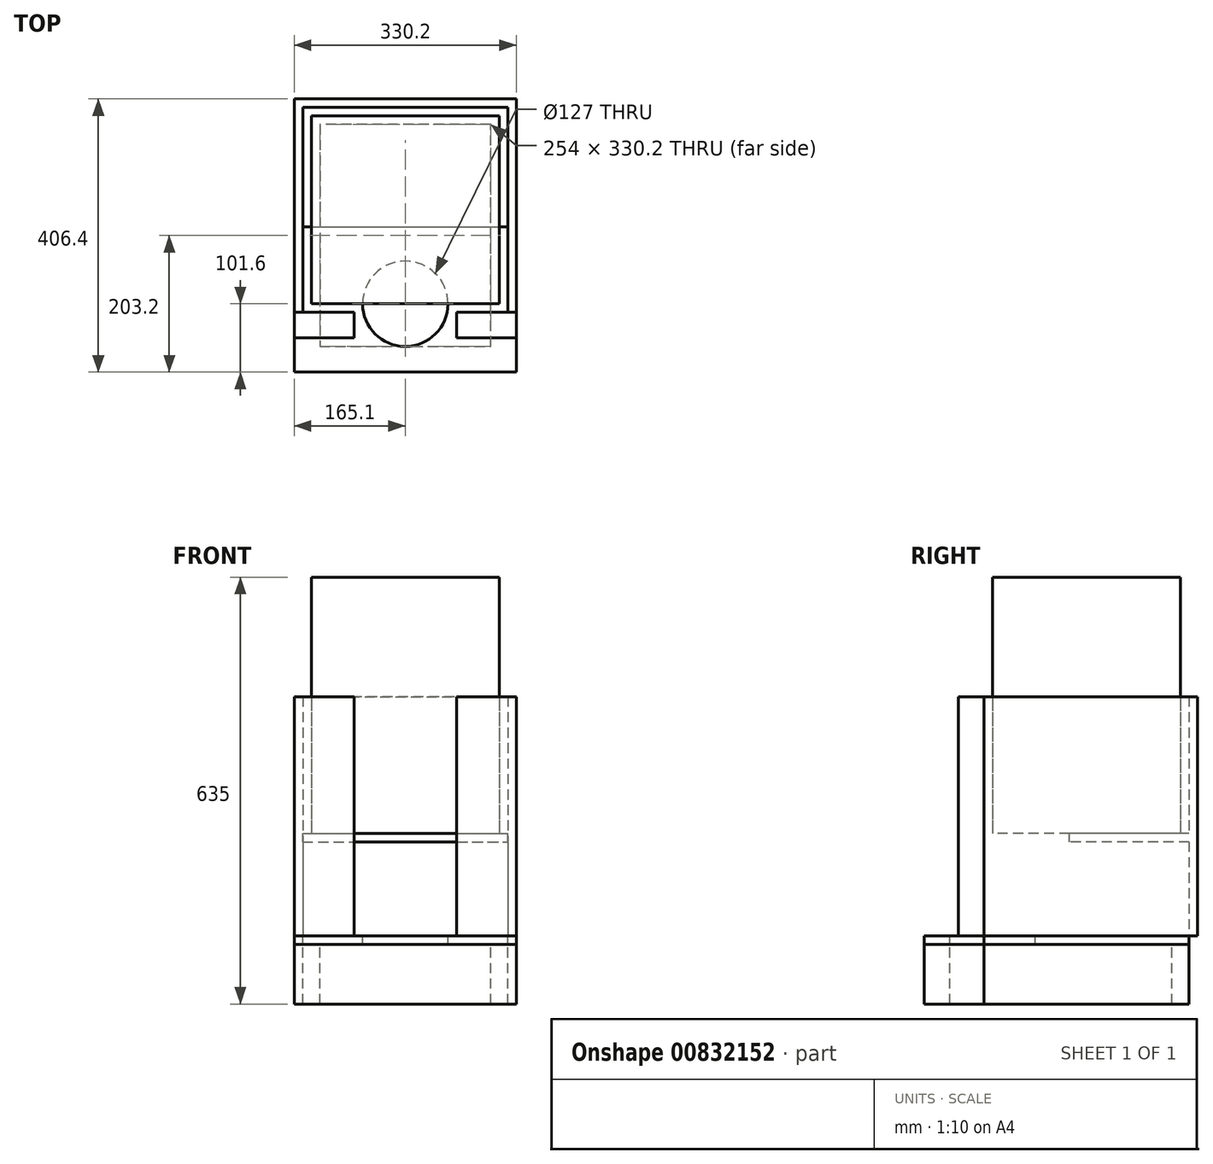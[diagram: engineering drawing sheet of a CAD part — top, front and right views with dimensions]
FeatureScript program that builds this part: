
annotation { "Feature Type Name" : "Feature", "Feature Type Description" : "" }
export const myFeature = defineFeature(function(context is Context, id is Id, definition is map)
    precondition{}
    {
        {
            var Q0;
            Q0=qCreatedBy(makeId("Top.planeOp"),FACE);
            var sketch = newSketch(context, id + "F0", { "sketchPlane" : qUnion([Q0])});
            skLineSegment(sketch, "E0", {"start": v(-165.1, 158.75) * mm, "end": v(-165.1, -158.75) * mm});
            skLineSegment(sketch, "E1", {"start": v(-152.4, -158.75) * mm, "end": v(-152.4, 146.05) * mm});
            skLineSegment(sketch, "E2", {"start": v(-152.4, 146.05) * mm, "end": v(152.4, 146.05) * mm});
            skLineSegment(sketch, "E3", {"start": v(152.4, 146.05) * mm, "end": v(152.4, -158.75) * mm});
            skLineSegment(sketch, "E4", {"start": v(165.1, -158.75) * mm, "end": v(165.1, 158.75) * mm});
            skLineSegment(sketch, "E5", {"start": v(165.1, 158.75) * mm, "end": v(-165.1, 158.75) * mm});
            skLineSegment(sketch, "E6", {"start": v(-152.4, 146.05) * mm, "end": v(-165.1, 146.05) * mm, "construction": true});
            skLineSegment(sketch, "E7", {"start": v(-152.4, 146.05) * mm, "end": v(-152.4, 158.75) * mm, "construction": true});
            skLineSegment(sketch, "E8", {"start": v(152.4, 146.05) * mm, "end": v(165.1, 146.05) * mm, "construction": true});
            skLineSegment(sketch, "E9", {"start": v(165.1, -158.75) * mm, "end": v(152.4, -158.75) * mm});
            skLineSegment(sketch, "E10", {"start": v(-152.4, -158.75) * mm, "end": v(-165.1, -158.75) * mm});
            skSolve(sketch);
        }
        {
            var Q0;
            Q0=makeQuery(id+"F0.imprint","IMPRINT",FACE,{"disambiguationData":[TD([[makeQuery(id+"F0.imprint","IMPRINT",EDGE,{"derivedFrom":sQuery(id+"F0.wireOp",EDGE,"E0")}),1.0]])]});
            extrude(context, id + "F1", {"entities" : qUnion([Q0]), "depth" : 355.6 * mm, "offsetDistance" : 25.4 * mm});
        }
        {
            var Q0;
            Q0=makeQuery(id+"F1.opExtrude","CAP_FACE",FACE,{"disambiguationData":[OSD([sQuery(id+"F0.wireOp",EDGE,"E0"),sQuery(id+"F0.wireOp",EDGE,"0fIPUXIq-EhR1-ypMC-8BNz-LEkebLUGr96P"),sQuery(id+"F0.wireOp",EDGE,"E1"),sQuery(id+"F0.wireOp",EDGE,"E2"),sQuery(id+"F0.wireOp",EDGE,"E3"),sQuery(id+"F0.wireOp",EDGE,"5RKXnEkp-DBpV-jKd3-7y9c-Gj4dhyzgzrL4"),sQuery(id+"F0.wireOp",EDGE,"E4"),sQuery(id+"F0.wireOp",EDGE,"E5"),sQuery(id+"F0.wireOp",EDGE,"tF0Km3Vx-QkFO-Dv44-yMe6-O5ppuTHv8n8t"),sQuery(id+"F0.wireOp",EDGE,"8CGNkZRK-zatz-oNot-bLPi-DGd3ZDuftX8x"),sQuery(id+"F0.wireOp",EDGE,"xndoMRrX-85Ha-ap0J-BBT2-as0rxpRnvae1"),sQuery(id+"F0.wireOp",EDGE,"YdPUmC4n-vJLc-jLnH-ZnBX-CcpX9o708nWJ")])],"isStart":true});
            var sketch = newSketch(context, id + "F2", { "sketchPlane" : qUnion([Q0])});
            skLineSegment(sketch, "E11.1", {"start": v(165.1, -158.75) * mm, "end": v(-165.1, -158.75) * mm});
            skLineSegment(sketch, "E12.top", {"start": v(-165.1, -158.75) * mm, "end": v(165.1, -158.75) * mm});
            skLineSegment(sketch, "E12.left", {"start": v(-165.1, 247.65) * mm, "end": v(-165.1, -158.75) * mm});
            skLineSegment(sketch, "E12.right", {"start": v(165.1, 247.65) * mm, "end": v(165.1, -158.75) * mm});
            skCircle(sketch, "E13", {"center": v(0, 146.05) * mm, "radius": 63.5 * mm});
            skLineSegment(sketch, "E14", {"start": v(165.1, 247.65) * mm, "end": v(-165.1, 247.65) * mm});
            skSolve(sketch);
        }
        {
            var Q0;
            Q0=makeQuery(id+"F2.imprint","IMPRINT",FACE,{"disambiguationData":[TD([[makeQuery(id+"F2.imprint","IMPRINT",EDGE,{"derivedFrom":sQuery(id+"F2.wireOp",EDGE,"E13")}),-1.0]])]});
            var Q1;
            {var subQ2=sQuery(id+"F2.wireOp",EDGE,"E12.top");Q1=makeQuery(id+"F2.imprint","IMPRINT",FACE,{"disambiguationData":[TD([[makeQuery(id+"F2.imprint","IMPRINT",EDGE,{"derivedFrom":subQ2}),-1.0]])]});}
            extrude(context, id + "F3", {"entities" : qUnion([Q0, Q1]), "operationType" : NewBodyOperationType.ADD, "depth" : 12.7 * mm, "offsetDistance" : 25.4 * mm});
        }
        {
            var Q0;
            Q0=makeQuery(id+"F3.opExtrude","CAP_FACE",FACE,{"disambiguationData":[OSD([sQuery(id+"F2.wireOp",EDGE,"E12.top"),sQuery(id+"F2.wireOp",EDGE,"E12.left"),sQuery(id+"F2.wireOp",EDGE,"E12.right"),sQuery(id+"F2.wireOp",EDGE,"E13"),sQuery(id+"F2.wireOp",EDGE,"E14")])],"isStart":false});
            var sketch = newSketch(context, id + "F4", { "sketchPlane" : qUnion([Q0])});
            skLineSegment(sketch, "E15.0", {"start": v(-165.1, -158.75) * mm, "end": v(-165.1, 247.65) * mm});
            skLineSegment(sketch, "E15.1", {"start": v(165.1, -158.75) * mm, "end": v(-165.1, -158.75) * mm});
            skLineSegment(sketch, "E15.2", {"start": v(165.1, 247.65) * mm, "end": v(165.1, -158.75) * mm});
            skLineSegment(sketch, "E16", {"start": v(-165.1, 247.65) * mm, "end": v(165.1, 247.65) * mm});
            skLineSegment(sketch, "E17.0", {"start": v(-127, -120.65) * mm, "end": v(-127, 209.55) * mm});
            skLineSegment(sketch, "E17.1", {"start": v(127, -120.65) * mm, "end": v(-127, -120.65) * mm});
            skLineSegment(sketch, "E17.2", {"start": v(127, 209.55) * mm, "end": v(127, -120.65) * mm});
            skLineSegment(sketch, "E17.3", {"start": v(-127, 209.55) * mm, "end": v(127, 209.55) * mm});
            skSolve(sketch);
        }
        {
            var Q0;
            Q0=makeQuery(id+"F4.imprint","IMPRINT",FACE,{"disambiguationData":[TD([[makeQuery(id+"F4.imprint","IMPRINT",EDGE,{"derivedFrom":sQuery(id+"F4.wireOp",EDGE,"E15.0")}),1.0]])]});
            extrude(context, id + "F5", {"entities" : qUnion([Q0]), "depth" : 88.9 * mm, "offsetDistance" : 25.4 * mm});
        }
        {
            var Q0;
            Q0=makeQuery(id+"F3.opExtrude","CAP_FACE",FACE,{"disambiguationData":[OSD([sQuery(id+"F2.wireOp",EDGE,"E12.top"),sQuery(id+"F2.wireOp",EDGE,"E12.left"),sQuery(id+"F2.wireOp",EDGE,"E12.right"),sQuery(id+"F2.wireOp",EDGE,"E13"),sQuery(id+"F2.wireOp",EDGE,"E14")])],"isStart":true});
            cPlane(context, id + "F6", {"entities" : qUnion([Q0]), "cplaneType" : CPlaneType.OFFSET, "offset" : 152.4 * mm, "width" : 152.4 * mm, "height" : 152.4 * mm});
        }
        {
            var Q0;
            Q0=qCreatedBy(id+"F6.planeOp",FACE);
            var sketch = newSketch(context, id + "F7", { "sketchPlane" : qUnion([Q0])});
            skCircle(sketch, "E18.0", {"center": v(0, -146.05) * mm, "radius": 63.5 * mm, "construction": true});
            skLineSegment(sketch, "E19.bottom", {"start": v(-139.7, 133.35) * mm, "end": v(139.7, 133.35) * mm});
            skLineSegment(sketch, "E19.top", {"start": v(-139.7, -146.05) * mm, "end": v(139.7, -146.05) * mm});
            skLineSegment(sketch, "E19.left", {"start": v(-139.7, 133.35) * mm, "end": v(-139.7, -146.05) * mm});
            skLineSegment(sketch, "E19.right", {"start": v(139.7, 133.35) * mm, "end": v(139.7, -146.05) * mm});
            skLineSegment(sketch, "E20", {"start": v(-139.7, 133.35) * mm, "end": v(-139.7, 146.05) * mm, "construction": true});
            skLineSegment(sketch, "E21", {"start": v(-139.7, 133.35) * mm, "end": v(-152.4, 133.35) * mm, "construction": true});
            skLineSegment(sketch, "E22", {"start": v(152.4, 133.35) * mm, "end": v(139.7, 133.35) * mm, "construction": true});
            skSolve(sketch);
        }
        {
            var Q0;
            Q0=makeQuery(id+"F7.imprint","IMPRINT",FACE,{"disambiguationData":[TD([[makeQuery(id+"F7.imprint","IMPRINT",EDGE,{"derivedFrom":sQuery(id+"F7.wireOp",EDGE,"E19.bottom")}),-1.0]])]});
            extrude(context, id + "F8", {"entities" : qUnion([Q0]), "depth" : 381 * mm, "offsetDistance" : 25.4 * mm});
        }
        {
            var Q0;
            Q0=makeQuery(id+"F3.opExtrude","CAP_FACE",FACE,{"disambiguationData":[OSD([sQuery(id+"F2.wireOp",EDGE,"E12.top"),sQuery(id+"F2.wireOp",EDGE,"E12.left"),sQuery(id+"F2.wireOp",EDGE,"E12.right"),sQuery(id+"F2.wireOp",EDGE,"E13"),sQuery(id+"F2.wireOp",EDGE,"E14")])],"isStart":true});
            var sketch = newSketch(context, id + "F9", { "sketchPlane" : qUnion([Q0])});
            skLineSegment(sketch, "E23.bottom", {"start": v(-165.1, -196.85) * mm, "end": v(-76.2, -196.85) * mm});
            skLineSegment(sketch, "E23.top", {"start": v(-165.1, -158.75) * mm, "end": v(-76.2, -158.75) * mm});
            skLineSegment(sketch, "E23.left", {"start": v(-165.1, -196.85) * mm, "end": v(-165.1, -158.75) * mm});
            skLineSegment(sketch, "E23.right", {"start": v(-76.2, -196.85) * mm, "end": v(-76.2, -158.75) * mm});
            skLineSegment(sketch, "E24.bottom", {"start": v(165.1, -196.85) * mm, "end": v(76.2, -196.85) * mm});
            skLineSegment(sketch, "E24.top", {"start": v(165.1, -158.75) * mm, "end": v(76.2, -158.75) * mm});
            skLineSegment(sketch, "E24.left", {"start": v(165.1, -196.85) * mm, "end": v(165.1, -158.75) * mm});
            skLineSegment(sketch, "E24.right", {"start": v(76.2, -196.85) * mm, "end": v(76.2, -158.75) * mm});
            skLineSegment(sketch, "E25", {"start": v(0, -247.65) * mm, "end": v(0, 0) * mm, "construction": true});
            skSolve(sketch);
        }
        {
            var Q0;
            Q0=makeQuery(id+"F9.imprint","IMPRINT",FACE,{"disambiguationData":[TD([[makeQuery(id+"F9.imprint","IMPRINT",EDGE,{"derivedFrom":sQuery(id+"F9.wireOp",EDGE,"E23.bottom")}),1.0]])]});
            var Q1;
            Q1=makeQuery(id+"F9.imprint","IMPRINT",FACE,{"disambiguationData":[TD([[makeQuery(id+"F9.imprint","IMPRINT",EDGE,{"derivedFrom":sQuery(id+"F9.wireOp",EDGE,"E24.bottom")}),-1.0]])]});
            var Q2;
            Q2=makeQuery(id+"F1.opExtrude","CAP_FACE",FACE,{"disambiguationData":[OSD([sQuery(id+"F0.wireOp",EDGE,"E0"),sQuery(id+"F0.wireOp",EDGE,"E1"),sQuery(id+"F0.wireOp",EDGE,"E2"),sQuery(id+"F0.wireOp",EDGE,"E3"),sQuery(id+"F0.wireOp",EDGE,"E4"),sQuery(id+"F0.wireOp",EDGE,"E5"),sQuery(id+"F0.wireOp",EDGE,"E9"),sQuery(id+"F0.wireOp",EDGE,"E10")])],"isStart":false});
            extrude(context, id + "F10", {"entities" : qUnion([Q0, Q1]), "endBound" : BoundingType.UP_TO_SURFACE, "depth" : 25.4 * mm, "endBoundEntityFace" : qUnion([Q2]), "offsetDistance" : 25.4 * mm});
        }
        {
            var Q0;
            Q0=qCreatedBy(id+"F6.planeOp",FACE);
            var sketch = newSketch(context, id + "F11", { "sketchPlane" : qUnion([Q0])});
            skLineSegment(sketch, "E26.0", {"start": v(-152.4, 146.05) * mm, "end": v(152.4, 146.05) * mm});
            skLineSegment(sketch, "E26.1", {"start": v(-152.4, -158.75) * mm, "end": v(-152.4, 146.05) * mm});
            skLineSegment(sketch, "E26.2", {"start": v(152.4, 146.05) * mm, "end": v(152.4, -158.75) * mm});
            skLineSegment(sketch, "E27", {"start": v(-152.4, -31.75) * mm, "end": v(152.4, -31.75) * mm});
            skSolve(sketch);
        }
        {
            var Q0;
            {var subQ0=sQuery(id+"F11.wireOp",EDGE,"E26.0");Q0=makeQuery(id+"F11.imprint","IMPRINT",FACE,{"disambiguationData":[TD([[makeQuery(id+"F11.imprint","IMPRINT",EDGE,{"derivedFrom":subQ0}),-1.0]])]});}
            extrude(context, id + "F12", {"entities" : qUnion([Q0]), "operationType" : NewBodyOperationType.ADD, "oppositeDirection" : true, "depth" : 12.7 * mm, "offsetDistance" : 25.4 * mm});
        }
    });
